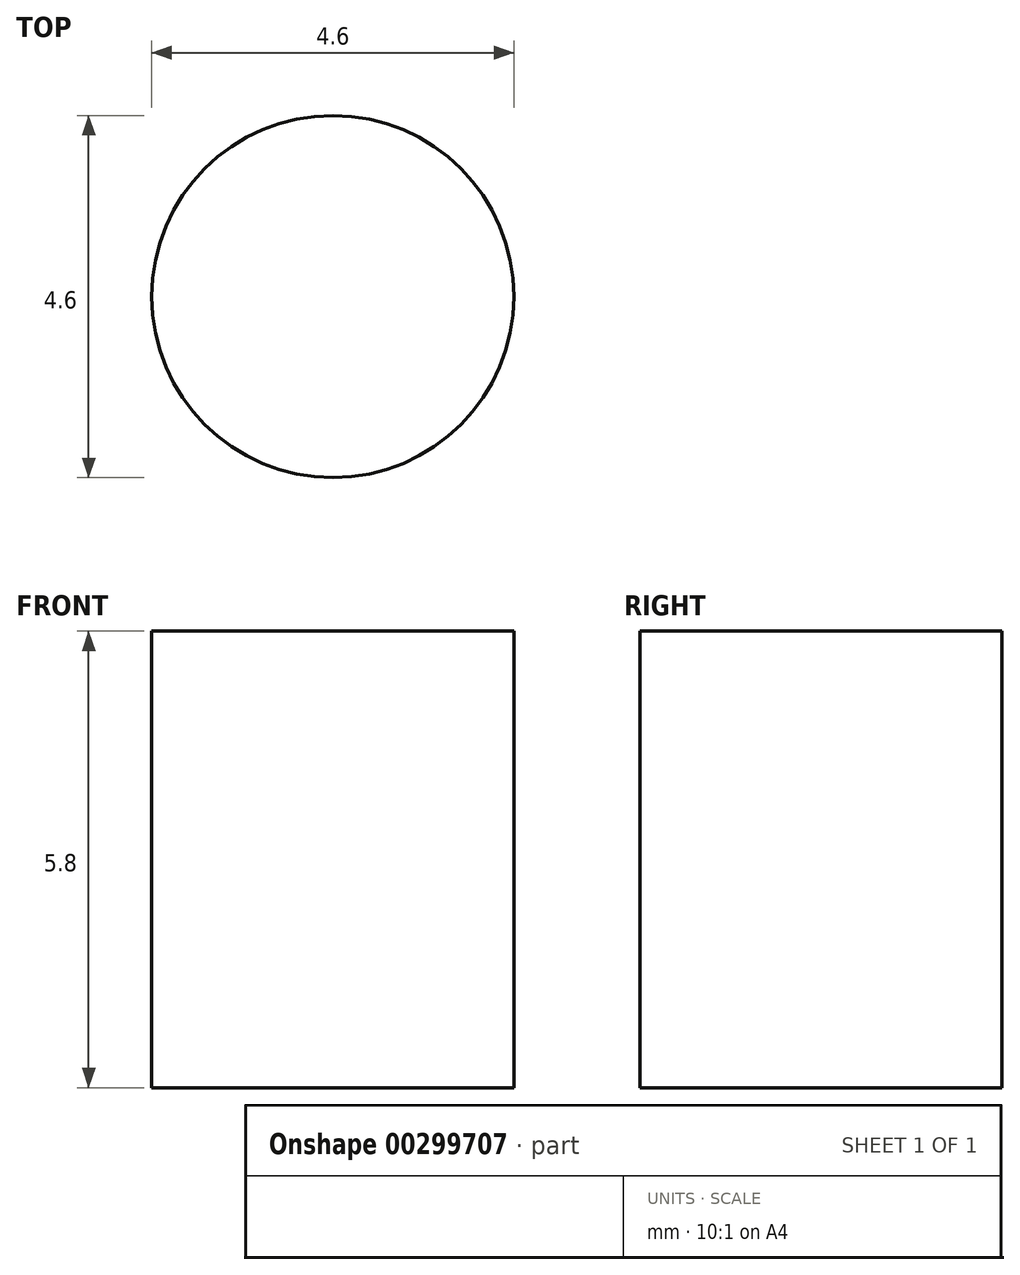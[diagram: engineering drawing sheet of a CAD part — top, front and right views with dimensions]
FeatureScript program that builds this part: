
annotation { "Feature Type Name" : "Feature", "Feature Type Description" : "" }
export const myFeature = defineFeature(function(context is Context, id is Id, definition is map)
    precondition{}
    {
        {
            var Q0;
            Q0=qCreatedBy(makeId("Top.planeOp"),FACE);
            var sketch = newSketch(context, id + "F0", { "sketchPlane" : qUnion([Q0])});
            skCircle(sketch, "E0", {"center": v(0, 0) * mm, "radius": 2.3 * mm});
            skSolve(sketch);
        }
        {
            var Q0;
            Q0=qSketchRegion(id+"F0",true);
            extrude(context, id + "F1", {"entities" : qUnion([Q0]), "depth" : 5.8 * mm});
        }
    });
